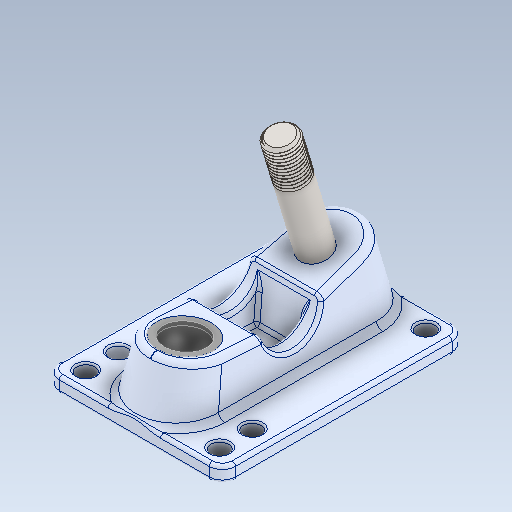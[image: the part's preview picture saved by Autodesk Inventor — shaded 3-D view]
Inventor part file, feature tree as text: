
AUTODESK INVENTOR PART (.ipt)
format: ipt  version: 2021 (Build 250183000, 183)  size: 1,024,000 bytes
history: mixed  units: in
note: dims shown in document units (in); Inventor stores cm internally (conversion verified against a paired STEP export)
features: revolve x1, other x1, thread x1, fillet x1, imported_body x1
ambient origin geometry x8: Origin, YZ Plane, XZ Plane, XY Plane, X Axis, Y Axis, Z Axis, Center Point
bodies: Solid1 (imported_parasolid), Solid2 (imported_parasolid), Solid3 (imported_parasolid), Solid4 (imported_parasolid)
feature tree (5):
  revolve  "Revolve1"  [1 undecoded]
  other  "Boss-Extrude2"
  thread  "Thread1"  [1 undecoded]
  fillet  "Fillet7"  [1 undecoded]
  imported_body  NMx_Import_Brep_tag  [imported B-rep: ~24 faces, bbox_mm=[26.0, 56.95363, 66.5]]
note: 3 required parameter values undecoded (feature->parameter linkage not recoverable at this tier; creation-order binding heuristic only, values carry confidence <= 0.55)
